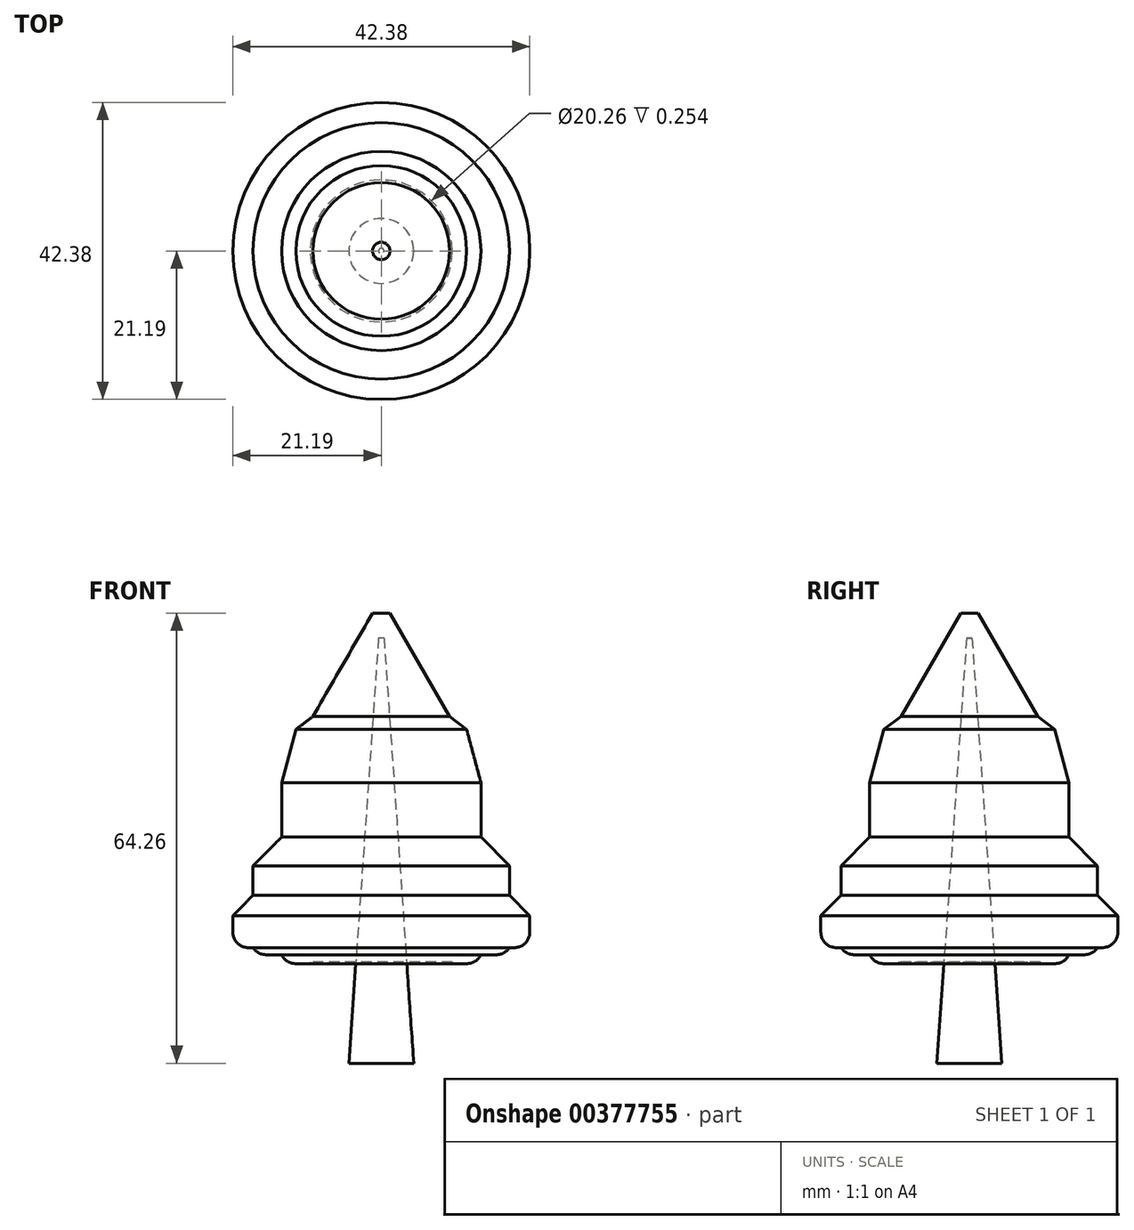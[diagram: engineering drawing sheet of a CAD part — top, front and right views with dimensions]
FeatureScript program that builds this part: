
annotation { "Feature Type Name" : "Feature", "Feature Type Description" : "" }
export const myFeature = defineFeature(function(context is Context, id is Id, definition is map)
    precondition{}
    {
        {
            var Q0;
            Q0=qCreatedBy(makeId("Top.planeOp"),FACE);
            var sketch = newSketch(context, id + "F0", { "sketchPlane" : qUnion([Q0])});
            skCircle(sketch, "E0", {"center": v(0, 0) * mm, "radius": 5.47 * mm});
            skCircle(sketch, "E1", {"center": v(0, 0) * mm, "radius": 21.2 * mm});
            skCircle(sketch, "E2", {"center": v(0, 0) * mm, "radius": 18.3 * mm});
            skCircle(sketch, "E3", {"center": v(0, 0) * mm, "radius": 14.22 * mm});
            skCircle(sketch, "E4", {"center": v(0, 0) * mm, "radius": 10.13 * mm});
            skSolve(sketch);
        }
        {
            var Q0;
            Q0=makeQuery(id+"F0.imprint","IMPRINT",FACE,{"disambiguationData":[TD([[makeQuery(id+"F0.imprint","IMPRINT",EDGE,{"derivedFrom":sQuery(id+"F0.wireOp",EDGE,"E0")}),1.0]])]});
            extrude(context, id + "F1", {"entities" : qUnion([Q0]), "depth" : 60.7 * mm});
        }
        {
            var Q0;
            Q0=makeQuery(id+"F1.opExtrude","CAP_EDGE",EDGE,{"disambiguationData":[OSD([sQuery(id+"F0.wireOp",EDGE,"E0")])],"isStart":false});
            chamfer(context, id + "F2", {"entities" : qUnion([Q0]), "chamferType" : ChamferType.OFFSET_ANGLE, "width" : 5.08 * mm, "oppositeDirection" : false, "angle" : 86 * degree, "tangentPropagation" : true});
        }
        {
            var Q0;
            Q0=makeQuery(id+"F0.imprint","IMPRINT",FACE,{"disambiguationData":[TD([[makeQuery(id+"F0.imprint","IMPRINT",EDGE,{"derivedFrom":sQuery(id+"F0.wireOp",EDGE,"E0")}),-1.0]])]});
            var Q1;
            Q1=makeQuery(id+"F0.imprint","IMPRINT",FACE,{"disambiguationData":[TD([[makeQuery(id+"F0.imprint","IMPRINT",EDGE,{"derivedFrom":sQuery(id+"F0.wireOp",EDGE,"E0")}),1.0]])]});
            extrude(context, id + "F3", {"entities" : qUnion([Q0, Q1]), "depth" : 64.26 * mm, "hasSecondDirection" : true, "secondDirectionOppositeDirection" : false, "secondDirectionDepth" : 14.48 * mm});
        }
        {
            var Q0;
            Q0=makeQuery(id+"F0.imprint","IMPRINT",FACE,{"disambiguationData":[TD([[makeQuery(id+"F0.imprint","IMPRINT",EDGE,{"derivedFrom":sQuery(id+"F0.wireOp",EDGE,"E3")}),1.0]])]});
            extrude(context, id + "F4", {"entities" : qUnion([Q0]), "operationType" : NewBodyOperationType.ADD, "depth" : 49.53 * mm, "hasSecondDirection" : true, "secondDirectionOppositeDirection" : false, "secondDirectionDepth" : 14.22 * mm});
        }
        {
            var Q0;
            Q0=makeQuery(id+"F0.imprint","IMPRINT",FACE,{"disambiguationData":[TD([[makeQuery(id+"F0.imprint","IMPRINT",EDGE,{"derivedFrom":sQuery(id+"F0.wireOp",EDGE,"E2")}),1.0]])]});
            extrude(context, id + "F5", {"entities" : qUnion([Q0]), "operationType" : NewBodyOperationType.ADD, "depth" : 33.27 * mm, "hasSecondDirection" : true, "secondDirectionOppositeDirection" : false, "secondDirectionDepth" : 15.5 * mm});
        }
        {
            var Q0;
            Q0=makeQuery(id+"F0.imprint","IMPRINT",FACE,{"disambiguationData":[TD([[makeQuery(id+"F0.imprint","IMPRINT",EDGE,{"derivedFrom":sQuery(id+"F0.wireOp",EDGE,"E1")}),1.0]])]});
            extrude(context, id + "F6", {"entities" : qUnion([Q0]), "operationType" : NewBodyOperationType.ADD, "depth" : 26.16 * mm, "hasSecondDirection" : true, "secondDirectionOppositeDirection" : false, "secondDirectionDepth" : 16.5 * mm});
        }
        {
            var Q0;
            Q0=makeQuery(id+"F3.opExtrude","CAP_EDGE",EDGE,{"disambiguationData":[OSD([sQuery(id+"F0.wireOp",EDGE,"E4")])],"isStart":false});
            chamfer(context, id + "F7", {"entities" : qUnion([Q0]), "chamferType" : ChamferType.OFFSET_ANGLE, "width" : 8.9 * mm, "oppositeDirection" : false, "angle" : 60 * degree, "tangentPropagation" : true});
        }
        {
            var Q0;
            Q0=makeQuery(id+"F4.opExtrude","CAP_EDGE",EDGE,{"disambiguationData":[OSD([sQuery(id+"F0.wireOp",EDGE,"E3")])],"isStart":false});
            chamfer(context, id + "F8", {"entities" : qUnion([Q0]), "chamferType" : ChamferType.OFFSET_ANGLE, "width" : 2.54 * mm, "oppositeDirection" : false, "angle" : 75 * degree, "tangentPropagation" : true});
        }
        {
            var Q0;
            Q0=makeQuery(id+"F5.opExtrude","CAP_EDGE",EDGE,{"disambiguationData":[OSD([sQuery(id+"F0.wireOp",EDGE,"E2")])],"isStart":false});
            var Q1;
            Q1=makeQuery(id+"F6.opExtrude","CAP_EDGE",EDGE,{"disambiguationData":[OSD([sQuery(id+"F0.wireOp",EDGE,"E1")])],"isStart":false});
            chamfer(context, id + "F9", {"entities" : qUnion([Q0, Q1]), "width" : 5.08 * mm, "tangentPropagation" : true});
        }
        {
            var Q0;
            Q0=makeQuery(id+"F6.opExtrude","CAP_EDGE",EDGE,{"disambiguationData":[OSD([sQuery(id+"F0.wireOp",EDGE,"E1")])],"isStart":true});
            var Q1;
            Q1=makeQuery(id+"F5.opExtrude","CAP_EDGE",EDGE,{"disambiguationData":[OSD([sQuery(id+"F0.wireOp",EDGE,"E2")])],"isStart":true});
            var Q2;
            Q2=makeQuery(id+"F4.opExtrude","CAP_EDGE",EDGE,{"disambiguationData":[OSD([sQuery(id+"F0.wireOp",EDGE,"E3")])],"isStart":true});
            fillet(context, id + "F10", {"entities" : qUnion([Q0, Q1, Q2]), "radius" : 2.2 * mm, "tangentPropagation" : true, "allowEdgeOverflow" : false});
        }
        {
            var Q0;
            {var subQ0=sQuery(id+"F0.wireOp",EDGE,"E3");Q0=makeQuery(id+"F8.opChamfer","BLEND_EDGE",EDGE,{"blendedFrom":[makeQuery(id+"F4.opExtrude","CAP_EDGE",EDGE,{"disambiguationData":[OSD([subQ0])],"isStart":false}),makeQuery(id+"F4.opExtrude","CAP_FACE",FACE,{"disambiguationData":[OSD([subQ0,sQuery(id+"F0.wireOp",EDGE,"E4")])],"isStart":false})],"blendedInto":[makeQuery(id+"F4.opExtrude","CAP_FACE",FACE,{"disambiguationData":[OSD([subQ0,sQuery(id+"F0.wireOp",EDGE,"E4")])],"isStart":false})]});}
            chamfer(context, id + "F11", {"entities" : qUnion([Q0]), "width" : 2.54 * mm, "tangentPropagation" : true});
        }
    });
